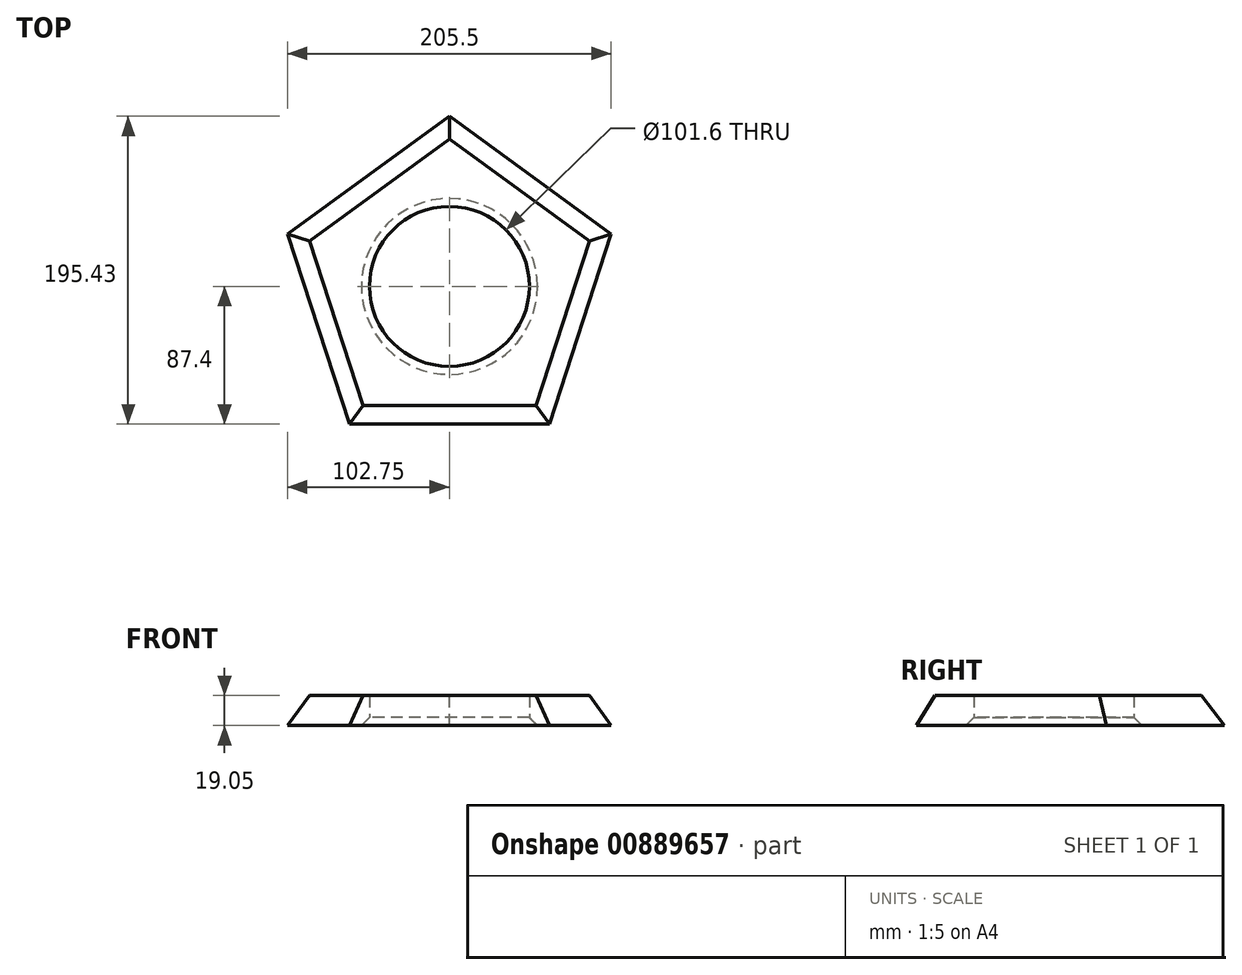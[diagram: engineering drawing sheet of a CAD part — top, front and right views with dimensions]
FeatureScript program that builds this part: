
annotation { "Feature Type Name" : "Feature", "Feature Type Description" : "" }
export const myFeature = defineFeature(function(context is Context, id is Id, definition is map)
    precondition{}
    {
        {
            var Q0;
            Q0=qCreatedBy(makeId("Top.planeOp"),FACE);
            var sketch = newSketch(context, id + "F0", { "sketchPlane" : qUnion([Q0])});
            skLineSegment(sketch, "E0", {"start": v(-102.75, 33.38) * mm, "end": v(-63.5, -87.4) * mm});
            skLineSegment(sketch, "E1", {"start": v(-102.75, 33.38) * mm, "end": v(0, 108.03) * mm});
            skLineSegment(sketch, "E2", {"start": v(0, 108.03) * mm, "end": v(102.75, 33.38) * mm});
            skLineSegment(sketch, "E3", {"start": v(102.75, 33.38) * mm, "end": v(63.5, -87.4) * mm});
            skLineSegment(sketch, "E4", {"start": v(63.5, -87.4) * mm, "end": v(-63.5, -87.4) * mm});
            skPoint(sketch, "E5", {"position": v(0, 0) * mm});
            skPoint(sketch, "E6", {"position": v(-83.12, -27) * mm});
            skPoint(sketch, "E7", {"position": v(83.12, -27) * mm});
            skCircle(sketch, "E8", {"center": v(0, 0) * mm, "radius": 50.8 * mm});
            skSolve(sketch);
        }
        {
            var Q0;
            Q0=makeQuery(id+"F0.imprint","IMPRINT",FACE,{"disambiguationData":[TD([[makeQuery(id+"F0.imprint","IMPRINT",EDGE,{"derivedFrom":sQuery(id+"F0.wireOp",EDGE,"E0")}),1.0]])]});
            extrude(context, id + "F1", {"entities" : qUnion([Q0]), "depth" : 19.05 * mm, "offsetDistance" : 25.4 * mm});
        }
        {
            var Q0;
            Q0=makeQuery(id+"F1.opExtrude","CAP_EDGE",EDGE,{"disambiguationData":[OSD([sQuery(id+"F0.wireOp",EDGE,"E4")])],"isStart":false});
            var Q1;
            Q1=makeQuery(id+"F1.opExtrude","CAP_EDGE",EDGE,{"disambiguationData":[OSD([sQuery(id+"F0.wireOp",EDGE,"E3")])],"isStart":false});
            var Q2;
            Q2=makeQuery(id+"F1.opExtrude","CAP_EDGE",EDGE,{"disambiguationData":[OSD([sQuery(id+"F0.wireOp",EDGE,"E2")])],"isStart":false});
            var Q3;
            Q3=makeQuery(id+"F1.opExtrude","CAP_EDGE",EDGE,{"disambiguationData":[OSD([sQuery(id+"F0.wireOp",EDGE,"E1")])],"isStart":false});
            var Q4;
            Q4=makeQuery(id+"F1.opExtrude","CAP_EDGE",EDGE,{"disambiguationData":[OSD([sQuery(id+"F0.wireOp",EDGE,"E0")])],"isStart":false});
            chamfer(context, id + "F2", {"entities" : qUnion([Q0, Q1, Q2, Q3, Q4]), "chamferType" : ChamferType.OFFSET_ANGLE, "width" : 19.05 * mm, "oppositeDirection" : false, "angle" : 31.7 * degree, "tangentPropagation" : true});
        }
        {
            var Q0;
            Q0=makeQuery(id+"F1.opExtrude","CAP_EDGE",EDGE,{"disambiguationData":[OSD([sQuery(id+"F0.wireOp",EDGE,"E8")])],"isStart":true});
            chamfer(context, id + "F3", {"entities" : qUnion([Q0]), "width" : 5.08 * mm, "tangentPropagation" : true});
        }
    });
